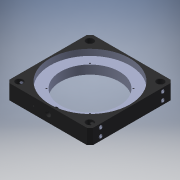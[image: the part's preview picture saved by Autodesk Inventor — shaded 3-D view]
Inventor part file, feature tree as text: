
AUTODESK INVENTOR PART (.ipt)
format: ipt  version: 2016 (Build 200138000, 138)  size: 482,304 bytes
history: native  units: mm
features: other x11, sketch x3
ambient origin geometry x8: Origin, YZ Plane, XZ Plane, XY Plane, X Axis, Y Axis, Z Axis, Center Point
bodies: Solid1 (feature_tree), Solid2 (feature_tree), Solid3 (feature_tree), Solid4 (feature_tree), Solid5 (feature_tree), Solid6 (feature_tree), Solid7 (feature_tree), Solid8 (feature_tree), Solid9 (feature_tree)
feature tree (14):
  other  "60mm-blank-cageplate-LCP03M-Nikon-MOD.ipt"
  other  "13108-001-1-solid1::60mm-blank-cageplate-LCP03M-Nikon-MOD.ipt"
  other  "SS4S019-1-1-solid1::60mm-blank-cageplate-LCP03M-Nikon-MOD.ipt"
  other  "SS4S019-1-2-solid1::60mm-blank-cageplate-LCP03M-Nikon-MOD.ipt"
  other  "SS4S019-1-3-solid1::60mm-blank-cageplate-LCP03M-Nikon-MOD.ipt"
  other  "SS4S019-1-4-solid1::60mm-blank-cageplate-LCP03M-Nikon-MOD.ipt"
  other  "SS4S019-1-5-solid1::60mm-blank-cageplate-LCP03M-Nikon-MOD.ipt"
  other  "SS4S019-1-6-solid1::60mm-blank-cageplate-LCP03M-Nikon-MOD.ipt"
  other  "SS4S019-1-7-solid1::60mm-blank-cageplate-LCP03M-Nikon-MOD.ipt"
  other  "SS4S019-1-8-solid1::60mm-blank-cageplate-LCP03M-Nikon-MOD.ipt"
  other  "TaggingFeature1"
  sketch  "Sketch1"  dims[d0=10.0mm]
  sketch  "Sketch2"
  sketch  "Sketch3"
